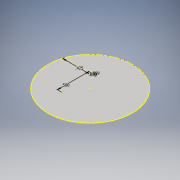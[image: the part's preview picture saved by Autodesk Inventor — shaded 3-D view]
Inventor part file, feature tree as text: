
AUTODESK INVENTOR PART (.ipt)
format: ipt  version: 2018 (Build 220112000, 112)  size: 110,592 bytes
history: native  units: in
note: dims shown in document units (in); Inventor stores cm internally (conversion verified against a paired STEP export)
features: sketch x2, extrude x1, fillet x1
ambient origin geometry x8: Origin, YZ Plane, XZ Plane, XY Plane, X Axis, Y Axis, Z Axis, Center Point
bodies: Solid1 (feature_tree)
feature tree (4):
  extrude  "Extrusion1"  Depth=0.0394in TaperAngle=0.0deg
  fillet  "Fillet1"  Radius=0.04in
  sketch  "Sketch2"  dims[d8=0.5in d10=0.0591in d14=0.0295in d15=0.0295in d16=0.425in]
  sketch  "Sketch1"  dims[d0=1.332in d1=0.0394in d2=0.0in d3=0.04in]
